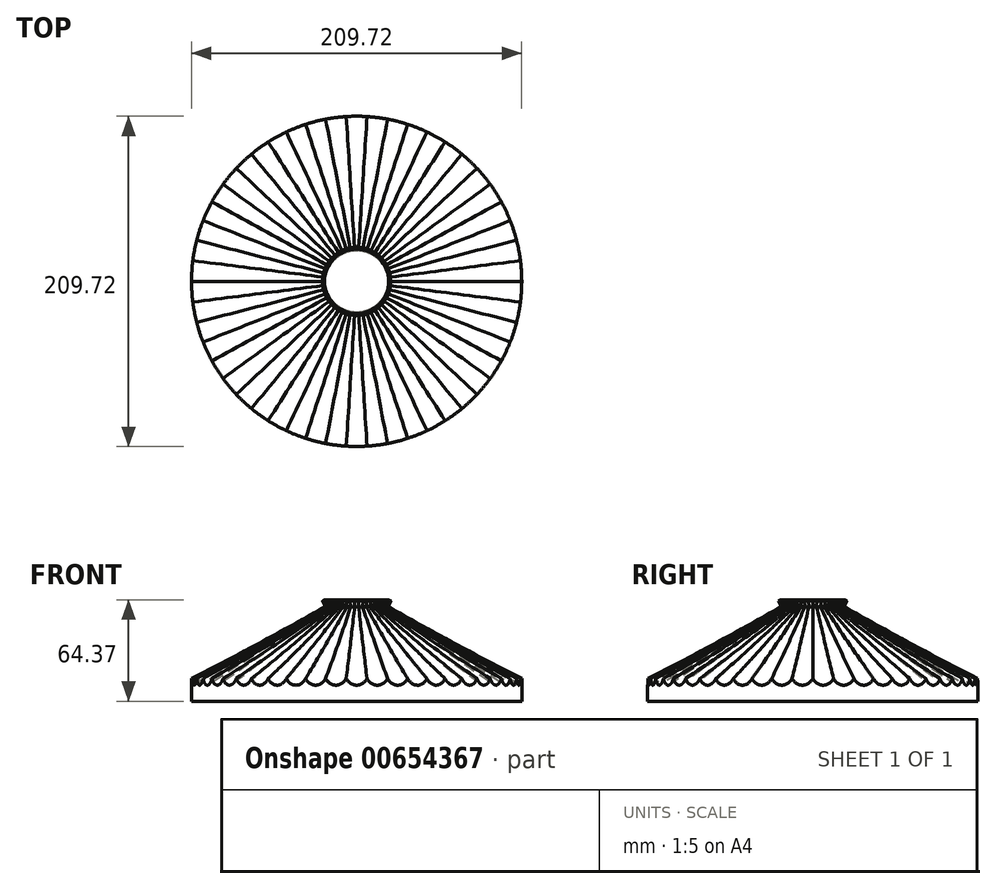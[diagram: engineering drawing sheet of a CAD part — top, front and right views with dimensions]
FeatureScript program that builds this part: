
annotation { "Feature Type Name" : "Feature", "Feature Type Description" : "" }
export const myFeature = defineFeature(function(context is Context, id is Id, definition is map)
    precondition{}
    {
        {
            var Q0;
            Q0=qCreatedBy(makeId("Right.planeOp"),FACE);
            var sketch = newSketch(context, id + "F0", { "sketchPlane" : qUnion([Q0])});
            skLineSegment(sketch, "E0", {"start": v(-22.07, 0) * mm, "end": v(-109.88, -47.84) * mm});
            skLineSegment(sketch, "E1", {"start": v(-109.88, -47.84) * mm, "end": v(-106.06, -54.87) * mm});
            skLineSegment(sketch, "E2", {"start": v(-106.06, -54.87) * mm, "end": v(-19.68, -4.4) * mm});
            skLineSegment(sketch, "E3", {"start": v(-19.68, -4.4) * mm, "end": v(-22.07, 0) * mm});
            skSolve(sketch);
        }
        {
            var Q0;
            Q0=makeQuery(id+"F0.imprint","IMPRINT",FACE,{"disambiguationData":[TD([[makeQuery(id+"F0.imprint","IMPRINT",EDGE,{"derivedFrom":sQuery(id+"F0.wireOp",EDGE,"E0")}),1.0]])]});
            var Q1;
            Q1=sQuery(id+"F0.wireOp",EDGE,"E0");
            revolve(context, id + "F1", {"entities" : qUnion([Q0]), "axis" : qUnion([Q1]), "revolveType" : RevolveType.FULL});
        }
        {
            var Q0;
            Q0=qCreatedBy(makeId("Right.planeOp"),FACE);
            var sketch = newSketch(context, id + "F2", { "sketchPlane" : qUnion([Q0])});
            skLineSegment(sketch, "E4", {"start": v(0, 0) * mm, "end": v(0, -46.27) * mm});
            skSolve(sketch);
        }
        {
            var Q0;
            Q0=makeQuery(id+"F1.opRevolve","SWEPT_BODY",BODY,{"disambiguationData":[OSD([sQuery(id+"F0.wireOp",EDGE,"E0"),sQuery(id+"F0.wireOp",EDGE,"E1"),sQuery(id+"F0.wireOp",EDGE,"E2"),sQuery(id+"F0.wireOp",EDGE,"E3")])]});
            var Q1;
            Q1=sQuery(id+"F2.wireOp",EDGE,"E4");
            circularPattern(context, id + "F3", {"operationType" : NewBodyOperationType.ADD, "entities" : qUnion([Q0]), "axis" : qUnion([Q1]), "angle" : 360 * degree, "instanceCount" : 50, "equalSpace" : true});
        }
        {
            var Q0;
            Q0=qCreatedBy(makeId("Right.planeOp"),FACE);
            var sketch = newSketch(context, id + "F4", { "sketchPlane" : qUnion([Q0])});
            skLineSegment(sketch, "E5", {"start": v(0, 0) * mm, "end": v(-20.4, 0) * mm});
            skLineSegment(sketch, "E6", {"start": v(-20.4, 0) * mm, "end": v(-104.86, -46.18) * mm});
            skLineSegment(sketch, "E7", {"start": v(-104.86, -46.18) * mm, "end": v(-104.86, -64.37) * mm});
            skLineSegment(sketch, "E8", {"start": v(-104.86, -64.37) * mm, "end": v(0, -64.37) * mm});
            skLineSegment(sketch, "E9", {"start": v(0, -64.37) * mm, "end": v(0, 0) * mm});
            skSolve(sketch);
        }
        {
            var Q0;
            Q0=makeQuery(id+"F4.imprint","IMPRINT",FACE,{"disambiguationData":[TD([[makeQuery(id+"F4.imprint","IMPRINT",EDGE,{"derivedFrom":sQuery(id+"F4.wireOp",EDGE,"E5")}),1.0]])]});
            var Q1;
            Q1=sQuery(id+"F4.wireOp",EDGE,"E9");
            revolve(context, id + "F5", {"entities" : qUnion([Q0]), "axis" : qUnion([Q1]), "revolveType" : RevolveType.FULL});
        }
        {
            var Q0;
            Q0=makeQuery(id+"F1.opRevolve","SWEPT_BODY",BODY,{"disambiguationData":[OSD([sQuery(id+"F0.wireOp",EDGE,"E0"),sQuery(id+"F0.wireOp",EDGE,"E1"),sQuery(id+"F0.wireOp",EDGE,"E2"),sQuery(id+"F0.wireOp",EDGE,"E3")])]});
            var Q1;
            Q1=makeQuery(id+"F5.opRevolve","SWEPT_BODY",BODY,{"disambiguationData":[OSD([sQuery(id+"F4.wireOp",EDGE,"E5"),sQuery(id+"F4.wireOp",EDGE,"E6"),sQuery(id+"F4.wireOp",EDGE,"E7"),sQuery(id+"F4.wireOp",EDGE,"E8"),sQuery(id+"F4.wireOp",EDGE,"E9")])]});
            booleanBodies(context, id + "F6", {"operationType" : BooleanOperationType.SUBTRACTION, "tools" : qUnion([Q0]), "targets" : qUnion([Q1])});
        }
    });
